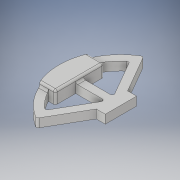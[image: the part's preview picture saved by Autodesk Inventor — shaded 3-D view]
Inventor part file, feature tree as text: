
AUTODESK INVENTOR PART (.ipt)
format: ipt  version: 2019 (Build 230136000, 136)  size: 204,288 bytes
history: native  units: mm
features: extrude x2, sketch x2, fillet x1
ambient origin geometry x8: Origin, YZ Plane, XZ Plane, XY Plane, X Axis, Y Axis, Z Axis, Center Point
bodies: Solide1 (feature_tree)
feature tree (5):
  extrude  "Extrusion1"  Depth=160.0mm
  extrude  "Extrusion2"  TaperAngle=60.0deg  [1 undecoded]
  fillet  "Congé1"  [1 undecoded]
  sketch  "Esquisse1"
  sketch  "Esquisse2"
note: 2 required parameter values undecoded (feature->parameter linkage not recoverable at this tier; creation-order binding heuristic only, values carry confidence <= 0.55)
